FCSTD DOCUMENT  (FreeCAD 0.17R13541 (Git))
Label: end_panel_jig
License: All rights reserved
LicenseURL: http://en.wikipedia.org/wiki/All_rights_reserved
objects: Sketcher::SketchObject×1
note: 1 computed .brp shape members not serialized (recipe doc carries the construction recipe); baked Part::Feature solids carry a one-line shape summary decoded from their .brp

FEATURE [Sketcher::SketchObject] Sketch
  sketch-geometry (21):
    g0: LineSegment StartX=9.75 StartY=76.25 StartZ=0 EndX=70.25 EndY=76.25 EndZ=0
    g1: LineSegment StartX=70.25 StartY=76.25 StartZ=0 EndX=70.25 EndY=53.75 EndZ=0
    g2: LineSegment StartX=70.25 StartY=53.75 StartZ=0 EndX=9.75 EndY=53.75 EndZ=0
    g3: LineSegment StartX=9.75 StartY=53.75 StartZ=0 EndX=9.75 EndY=76.25 EndZ=0
    g4: LineSegment StartX=0 StartY=86.25 StartZ=0 EndX=80 EndY=86.25 EndZ=0
    g5: LineSegment StartX=80 StartY=86.25 StartZ=0 EndX=80 EndY=0 EndZ=0
    g6: LineSegment StartX=80 StartY=0 StartZ=0 EndX=0 EndY=0 EndZ=0
    g7: LineSegment StartX=0 StartY=0 StartZ=0 EndX=0 EndY=86.25 EndZ=0
    g8: LineSegment [constr] StartX=9.75 StartY=76.25 StartZ=0 EndX=70.25 EndY=53.75 EndZ=0
    g9: LineSegment [constr] StartX=9.75 StartY=53.75 StartZ=0 EndX=70.25 EndY=76.25 EndZ=0
    g10: GeomPoint X=40 Y=65 Z=0
    g11: Circle CenterX=17.5 CenterY=20 CenterZ=0 NormalX=0 NormalY=0 NormalZ=1 AngleXU=0 Radius=3.1
    g12: Circle CenterX=62.5 CenterY=20 CenterZ=0 NormalX=0 NormalY=0 NormalZ=1 AngleXU=0 Radius=3.1
    g13: LineSegment [constr] StartX=17.5 StartY=20 StartZ=0 EndX=62.5 EndY=20 EndZ=0
    g14: LineSegment [constr] StartX=62.5 StartY=20 StartZ=0 EndX=80 EndY=20 EndZ=0
    g15: LineSegment [constr] StartX=17.5 StartY=20 StartZ=0 EndX=0 EndY=20 EndZ=0
    g16: LineSegment [constr] StartX=40 StartY=65 StartZ=0 EndX=0 EndY=65 EndZ=0
    g17: LineSegment [constr] StartX=40 StartY=65 StartZ=0 EndX=80 EndY=65 EndZ=0
    g18: Circle CenterX=40 CenterY=43.75 CenterZ=0 NormalX=0 NormalY=0 NormalZ=1 AngleXU=0 Radius=0.25
    g19: LineSegment [constr] StartX=0 StartY=43.75 StartZ=0 EndX=40 EndY=43.75 EndZ=0
    g20: LineSegment [constr] StartX=40 StartY=43.75 StartZ=0 EndX=80 EndY=43.75 EndZ=0
  constraints (58):
    c: Coincident(g0,g1)
    c: Coincident(g1,g2)
    c: Coincident(g2,g3)
    c: Coincident(g3,g0)
    c: Horizontal(g0)
    c: Horizontal(g2)
    c: Vertical(g1)
    c: Vertical(g3)
    c: DistanceX(g0,g0) = 60.5
    c: DistanceY(g3,g3) = 22.5
    c: Coincident(g4,g5)
    c: Coincident(g5,g6)
    c: Coincident(g6,g7)
    c: Coincident(g7,g4)
    c: Horizontal(g4)
    c: Horizontal(g6)
    c: Vertical(g5)
    c: Vertical(g7)
    c: DistanceX(g4,g4) = 80
    c: DistanceY(g0,g4) = 10
    c: Coincident(g8,g1)
    c: Coincident(g9,g2)
    c: Coincident(g9,g0)
    c: PointOnObject(g10,g8)
    c: PointOnObject(g10,g9)
    c: Coincident(g13,g12)
    c: Horizontal(g13)
    c: Coincident(g14,g12)
    c: PointOnObject(g14,g5)
    c: Horizontal(g14)
    c: Coincident(g15,g11)
    c: PointOnObject(g15,g7)
    c: Horizontal(g15)
    c: Equal(g15,g14)
    c: DistanceY(g12,g10) = 45
    c: DistanceY(g5,g12) = 20
    c: Coincident(g11,g13)
    c: Equal(g11,g12)
    c: Radius(g11) = 3.1
    c: DistanceX(g13,g13) = 45
    c: Coincident(g16,g10)
    c: PointOnObject(g16,g7)
    c: Horizontal(g16)
    c: Coincident(g17,g10)
    c: PointOnObject(g17,g5)
    c: Horizontal(g17)
    c: Equal(g16,g17)
    c: Coincident(g-1,g6)
    c: Coincident(g8,g0)
    c: DistanceY(g18,g1) = 10
    c: PointOnObject(g19,g7)
    c: Coincident(g19,g18)
    c: Horizontal(g19)
    c: PointOnObject(g20,g5)
    c: Horizontal(g20)
    c: Equal(g19,g20)
    c: Radius(g18) = 0.25
    c: Coincident(g20,g18)
